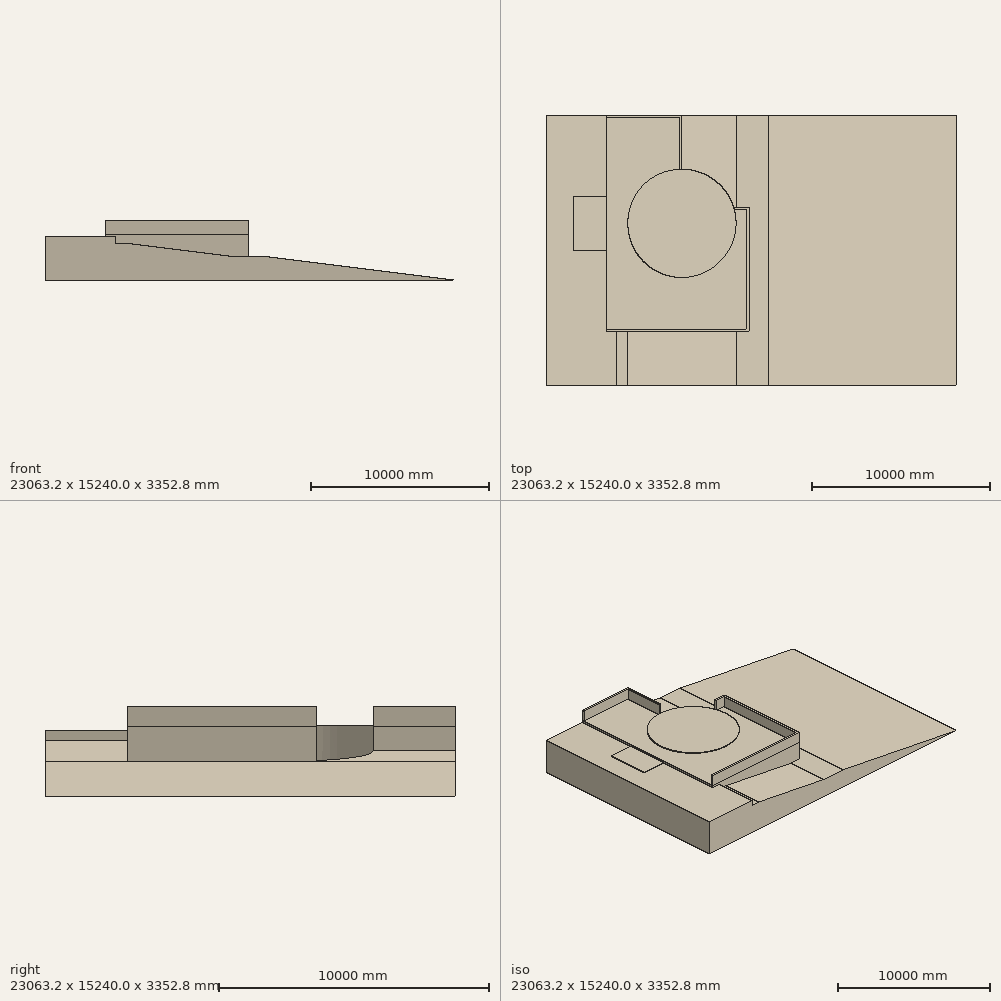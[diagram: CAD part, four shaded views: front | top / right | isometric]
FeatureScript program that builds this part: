
annotation { "Feature Type Name" : "Feature", "Feature Type Description" : "" }
export const myFeature = defineFeature(function(context is Context, id is Id, definition is map)
    precondition{}
    {
        {
            var Q0;
            Q0=qCreatedBy(makeId("Top.planeOp"),FACE);
            var sketch = newSketch(context, id + "F0", { "sketchPlane" : qUnion([Q0])});
            skCircle(sketch, "E0", {"center": v(0, 0) * mm, "radius": 3048 * mm});
            skSolve(sketch);
        }
        {
            var Q0;
            Q0=makeQuery(id+"F0.imprint","IMPRINT",FACE,{"disambiguationData":[TD([[makeQuery(id+"F0.imprint","IMPRINT",EDGE,{"derivedFrom":sQuery(id+"F0.wireOp",EDGE,"E0")}),1.0]])]});
            extrude(context, id + "F1", {"entities" : qUnion([Q0]), "depth" : 1320.8 * mm, "offsetDistance" : 25.4 * mm});
        }
        {
            var Q0;
            Q0=qCreatedBy(makeId("Front.planeOp"),FACE);
            var sketch = newSketch(context, id + "F2", { "sketchPlane" : qUnion([Q0])});
            skLineSegment(sketch, "E1", {"start": v(-3048, 0) * mm, "end": v(-3048, 1320.8) * mm});
            skLineSegment(sketch, "E2", {"start": v(3048, 1320.8) * mm, "end": v(3048, 0) * mm});
            skLineSegment(sketch, "E3", {"start": v(-3048, 762) * mm, "end": v(-3657.6, 762) * mm});
            skLineSegment(sketch, "E4", {"start": v(-3048, 762) * mm, "end": v(3048, 0) * mm});
            skLineSegment(sketch, "E5", {"start": v(-3657.6, 1117.6) * mm, "end": v(-5459.43, 1117.6) * mm});
            skLineSegment(sketch, "E6", {"start": v(-3657.6, 1117.6) * mm, "end": v(-3657.6, 762) * mm});
            skLineSegment(sketch, "E7", {"start": v(-5459.43, 1117.6) * mm, "end": v(-7620, 1117.6) * mm});
            skLineSegment(sketch, "E8", {"start": v(-7620, 1117.6) * mm, "end": v(-7620, -1320.8) * mm});
            skLineSegment(sketch, "E9", {"start": v(-7620, -1320.8) * mm, "end": v(15443.2, -1320.8) * mm});
            skLineSegment(sketch, "E10", {"start": v(3048, 0) * mm, "end": v(4876.8, 0) * mm});
            skLineSegment(sketch, "E11", {"start": v(4876.8, 0) * mm, "end": v(15443.2, -1320.8) * mm});
            skPoint(sketch, "E12.orphan", {"position": v(-7620, 762) * mm});
            skLineSegment(sketch, "E13.0", {"start": v(-3048, 0) * mm, "end": v(3048, 0) * mm, "construction": true});
            skSolve(sketch);
        }
        {
            var Q0;
            Q0=qSketchRegion(id+"F2",true);
            extrude(context, id + "F3", {"entities" : qUnion([Q0]), "depth" : 9144 * mm, "offsetDistance" : 25.4 * mm});
        }
        {
            var Q0;
            Q0=makeQuery(id+"F3.opExtrude","CAP_FACE",FACE,{"disambiguationData":[OSD([sQuery(id+"F2.wireOp",EDGE,"E3"),sQuery(id+"F2.wireOp",EDGE,"E4"),sQuery(id+"F2.wireOp",EDGE,"E5"),sQuery(id+"F2.wireOp",EDGE,"E6"),sQuery(id+"F2.wireOp",EDGE,"E7"),sQuery(id+"F2.wireOp",EDGE,"E8"),sQuery(id+"F2.wireOp",EDGE,"E9"),sQuery(id+"F2.wireOp",EDGE,"E10"),sQuery(id+"F2.wireOp",EDGE,"E11")])],"isStart":true});
            extrude(context, id + "F4", {"entities" : qUnion([Q0]), "operationType" : NewBodyOperationType.ADD, "depth" : 6096 * mm, "offsetDistance" : 25.4 * mm});
        }
        {
            var Q0;
            Q0=makeQuery(id+"F1.opExtrude","CAP_FACE",FACE,{"disambiguationData":[OSD([sQuery(id+"F0.wireOp",EDGE,"E0")])],"isStart":false});
            cPlane(context, id + "F5", {"entities" : qUnion([Q0]), "cplaneType" : CPlaneType.OFFSET, "offset" : 50.8 * mm, "oppositeDirection" : true, "width" : 152.4 * mm, "height" : 152.4 * mm});
        }
        {
            var Q0;
            Q0=qCreatedBy(id+"F5.planeOp",FACE);
            var sketch = newSketch(context, id + "F6", { "sketchPlane" : qUnion([Q0])});
            skCircle(sketch, "E14.0", {"center": v(0, 0) * mm, "radius": 3048 * mm});
            skLineSegment(sketch, "E15.bottom", {"start": v(-4267.2, 6096) * mm, "end": v(0, 6096) * mm});
            skLineSegment(sketch, "E15.top", {"start": v(-4267.2, -6096) * mm, "end": v(3810, -6096) * mm});
            skLineSegment(sketch, "E15.left", {"start": v(-4267.2, 6096) * mm, "end": v(-4267.2, -6096) * mm});
            skLineSegment(sketch, "E15.right", {"start": v(3810, 914.4) * mm, "end": v(3810, -6096) * mm});
            skLineSegment(sketch, "E16", {"start": v(0, 3048) * mm, "end": v(0, 6096) * mm});
            skLineSegment(sketch, "E17", {"start": v(2907.6, 914.4) * mm, "end": v(3810, 914.4) * mm});
            skSolve(sketch);
        }
        {
            var Q0;
            Q0=makeQuery(id+"F6.imprint","IMPRINT",FACE,{"disambiguationData":[TD([[makeQuery(id+"F6.imprint","IMPRINT",EDGE,{"derivedFrom":sQuery(id+"F6.wireOp",EDGE,"E15.bottom")}),-1.0]])]});
            extrude(context, id + "F7", {"entities" : qUnion([Q0]), "endBound" : BoundingType.UP_TO_NEXT, "oppositeDirection" : true, "depth" : 25.4 * mm, "offsetDistance" : 25.4 * mm});
        }
        {
            var Q0;
            Q0=makeQuery(id+"F7.opExtrude","CAP_FACE",FACE,{"disambiguationData":[OSD([sQuery(id+"F6.wireOp",EDGE,"E14.0"),sQuery(id+"F6.wireOp",EDGE,"E15.bottom"),sQuery(id+"F6.wireOp",EDGE,"E15.top"),sQuery(id+"F6.wireOp",EDGE,"E15.left"),sQuery(id+"F6.wireOp",EDGE,"E15.right"),sQuery(id+"F6.wireOp",EDGE,"E16"),sQuery(id+"F6.wireOp",EDGE,"E17")])],"isStart":true});
            var sketch = newSketch(context, id + "F8", { "sketchPlane" : qUnion([Q0])});
            skLineSegment(sketch, "E18.0.0", {"start": v(3810, 914.4) * mm, "end": v(2907.6, 914.4) * mm});
            skArc(sketch, "E18.0.1", {"start": v(2907.6, 914.4) * mm, "mid": v(-1803.22, -2457.38) * mm, "end": v(0, 3048) * mm});
            skLineSegment(sketch, "E18.0.2", {"start": v(0, 3048) * mm, "end": v(0, 6096) * mm});
            skLineSegment(sketch, "E18.0.3", {"start": v(0, 6096) * mm, "end": v(-4267.2, 6096) * mm});
            skLineSegment(sketch, "E18.0.4", {"start": v(-4267.2, 6096) * mm, "end": v(-4267.2, -6096) * mm});
            skLineSegment(sketch, "E18.0.5", {"start": v(-4267.2, -6096) * mm, "end": v(3810, -6096) * mm});
            skLineSegment(sketch, "E18.0.6", {"start": v(3810, -6096) * mm, "end": v(3810, 914.4) * mm});
            skLineSegment(sketch, "E19.0", {"start": v(3657.6, -5943.6) * mm, "end": v(3657.6, 762) * mm});
            skLineSegment(sketch, "E19.1", {"start": v(-4267.2, -5943.6) * mm, "end": v(3657.6, -5943.6) * mm});
            skLineSegment(sketch, "E19.3", {"start": v(-152.4, 3044.19) * mm, "end": v(-152.4, 5943.6) * mm});
            skLineSegment(sketch, "E19.4", {"start": v(-152.4, 5943.6) * mm, "end": v(-4267.2, 5943.6) * mm});
            skLineSegment(sketch, "E19.5", {"start": v(3657.6, 762) * mm, "end": v(2951.21, 762) * mm});
            skSolve(sketch);
        }
        {
            var Q0;
            {var subQ4=sQuery(id+"F8.wireOp",EDGE,"E18.0.0");Q0=makeQuery(id+"F8.imprint","IMPRINT",FACE,{"disambiguationData":[TD([[makeQuery(id+"F8.imprint","IMPRINT",EDGE,{"derivedFrom":subQ4}),-1.0]])]});}
            var Q1;
            {var subQ3=sQuery(id+"F8.wireOp",EDGE,"E18.0.2");Q1=makeQuery(id+"F8.imprint","IMPRINT",FACE,{"disambiguationData":[TD([[makeQuery(id+"F8.imprint","IMPRINT",EDGE,{"derivedFrom":subQ3}),1.0]])]});}
            extrude(context, id + "F9", {"entities" : qUnion([Q0, Q1]), "depth" : 762 * mm, "offsetDistance" : 25.4 * mm});
        }
        {
            var Q0;
            {var subQ0=sQuery(id+"F2.wireOp",EDGE,"E7");var subQ1=sQuery(id+"F2.wireOp",EDGE,"E5");Q0=makeQuery(id+"F4.boolean.opBoolean","MERGE",FACE,{"derivedFrom":[makeQuery(id+"F3.opExtrude","SWEPT_FACE",FACE,{"disambiguationData":[OSD([subQ1,subQ0])]}),makeQuery(id+"F4.opExtrude","SWEPT_FACE",FACE,{"disambiguationData":[OSD([subQ1,subQ0])]})]});}
            var sketch = newSketch(context, id + "F10", { "sketchPlane" : qUnion([Q0])});
            skLineSegment(sketch, "E20.bottom", {"start": v(-4267.2, 1524) * mm, "end": v(-6096, 1524) * mm});
            skLineSegment(sketch, "E20.top", {"start": v(-4267.2, -1524) * mm, "end": v(-6096, -1524) * mm});
            skLineSegment(sketch, "E20.left", {"start": v(-4267.2, 1524) * mm, "end": v(-4267.2, -1524) * mm});
            skLineSegment(sketch, "E20.right", {"start": v(-6096, 1524) * mm, "end": v(-6096, -1524) * mm});
            skSolve(sketch);
        }
        {
            var Q0;
            Q0=qSketchRegion(id+"F10",true);
            extrude(context, id + "F11", {"entities" : qUnion([Q0]), "depth" : 50.8 * mm, "offsetDistance" : 25.4 * mm});
        }
    });
